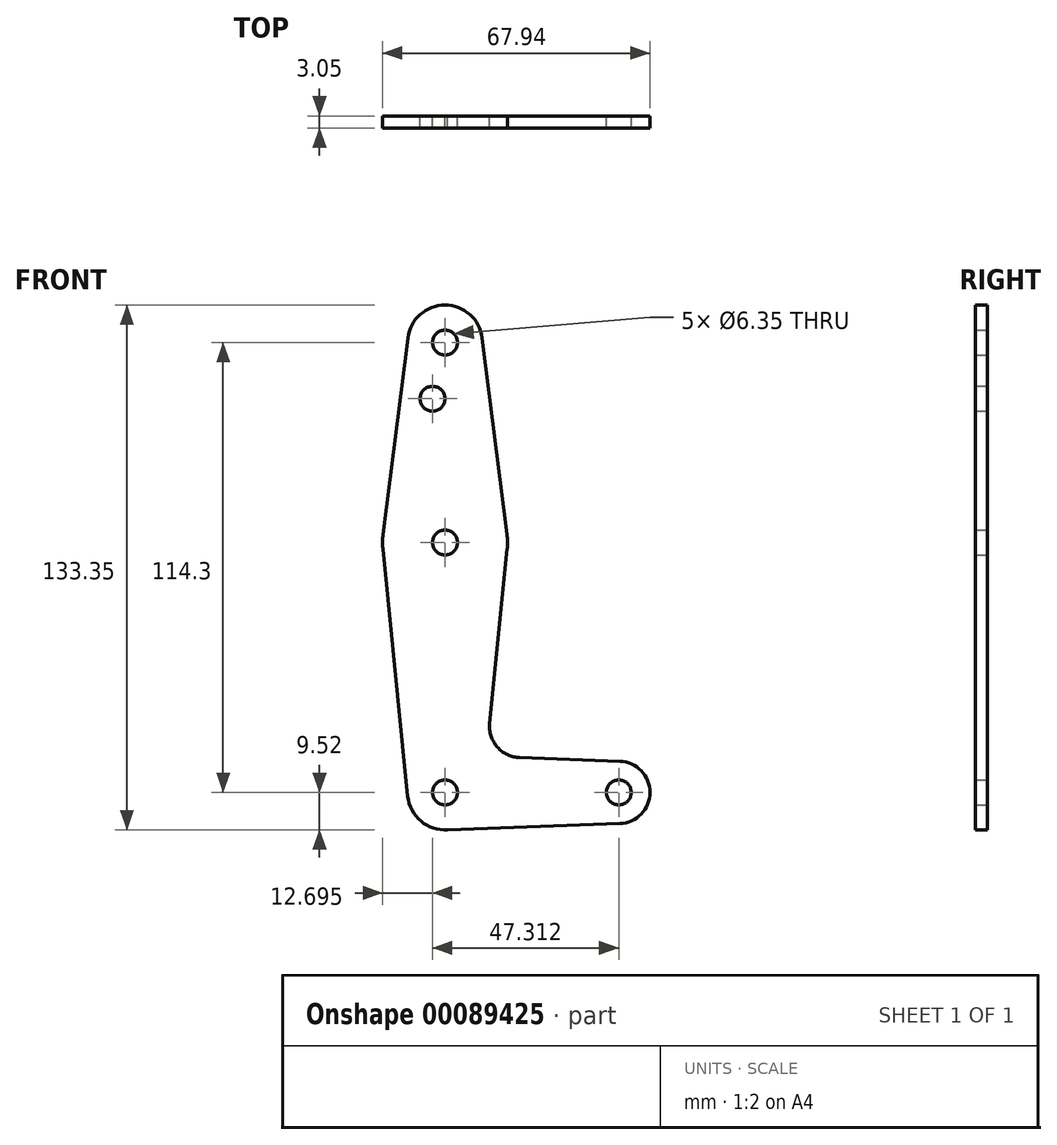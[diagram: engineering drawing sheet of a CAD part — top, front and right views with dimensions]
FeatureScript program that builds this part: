
annotation { "Feature Type Name" : "Feature", "Feature Type Description" : "" }
export const myFeature = defineFeature(function(context is Context, id is Id, definition is map)
    precondition{}
    {
        {
            var Q0;
            Q0=qCreatedBy(makeId("Front.planeOp"),FACE);
            var sketch = newSketch(context, id + "F0", { "sketchPlane" : qUnion([Q0])});
            skLineSegment(sketch, "E0", {"start": v(0, 114.3) * mm, "end": v(0, 0) * mm});
            skLineSegment(sketch, "E1", {"start": v(0, 0) * mm, "end": v(44.14, 0) * mm});
            skCircle(sketch, "E2", {"center": v(0, 114.3) * mm, "radius": 9.53 * mm});
            skCircle(sketch, "E3", {"center": v(0, 63.5) * mm, "radius": 15.88 * mm});
            skCircle(sketch, "E4", {"center": v(0, 0) * mm, "radius": 9.53 * mm});
            skCircle(sketch, "E5", {"center": v(44.14, 0) * mm, "radius": 7.94 * mm});
            skLineSegment(sketch, "E6", {"start": v(-9.45, 115.5) * mm, "end": v(-15.75, 65.48) * mm});
            skLineSegment(sketch, "E7", {"start": v(9.45, 115.5) * mm, "end": v(15.75, 65.48) * mm});
            skCircle(sketch, "E8", {"center": v(-3.18, 100.03) * mm, "radius": 3.18 * mm});
            skCircle(sketch, "E9", {"center": v(0, 114.3) * mm, "radius": 3.18 * mm});
            skCircle(sketch, "E10", {"center": v(44.14, 0) * mm, "radius": 3.18 * mm});
            skLineSegment(sketch, "E11", {"start": v(-15.8, 61.91) * mm, "end": v(-9.48, -0.95) * mm});
            skLineSegment(sketch, "E12", {"start": v(15.8, 61.91) * mm, "end": v(11.34, 17.59) * mm});
            skLineSegment(sketch, "E13", {"start": v(44.42, 7.93) * mm, "end": v(18.97, 8.85) * mm});
            skPoint(sketch, "E14.newPointA", {"position": v(9.48, -0.95) * mm});
            skArc(sketch, "E14.filletArc", {"start": v(11.34, 17.59) * mm, "mid": v(13.26, 11.57) * mm, "end": v(18.97, 8.85) * mm});
            skLineSegment(sketch, "E15", {"start": v(0, -9.53) * mm, "end": v(44.42, -7.93) * mm});
            skCircle(sketch, "E16", {"center": v(0, 0) * mm, "radius": 3.18 * mm});
            skCircle(sketch, "E17", {"center": v(0, 63.5) * mm, "radius": 3.18 * mm});
            skSolve(sketch);
        }
        {
            var Q0;
            Q0 = qSketchRegion(id + "F0", true);
            extrude(context, id + "F1", {"entities" : qUnion([Q0]), "depth" : 3.05 * mm});
        }
        {
            var Q0;
            Q0 = qSketchRegion(id + "F0", true);
            extrude(context, id + "F2", {"entities" : qUnion([Q0]), "operationType" : NewBodyOperationType.ADD, "depth" : 3.05 * mm});
        }
        {
            var Q0;
            Q0 = qSketchRegion(id + "F0", true);
            var Q1;
            {var subQ0=sQuery(id+"F0.wireOp",EDGE,"E4");var subQ1=sQuery(id+"F0.wireOp",EDGE,"E0");var subQ2=makeQuery(id+"F0.imprint","INTERSECT",VERTEX,{"derivedFrom":[subQ1,subQ0]});Q1=makeQuery(id+"F0.imprint","IMPRINT",FACE,{"disambiguationData":[TD([[makeQuery(id+"F0.imprint","IMPRINT",EDGE,{"disambiguationData":[TD([[subQ2,-1.0]])],"derivedFrom":subQ1}),1.0]])]});}
            extrude(context, id + "F3", {"entities" : qUnion([Q0, Q1]), "operationType" : NewBodyOperationType.ADD, "depth" : 3.05 * mm});
        }
    });
